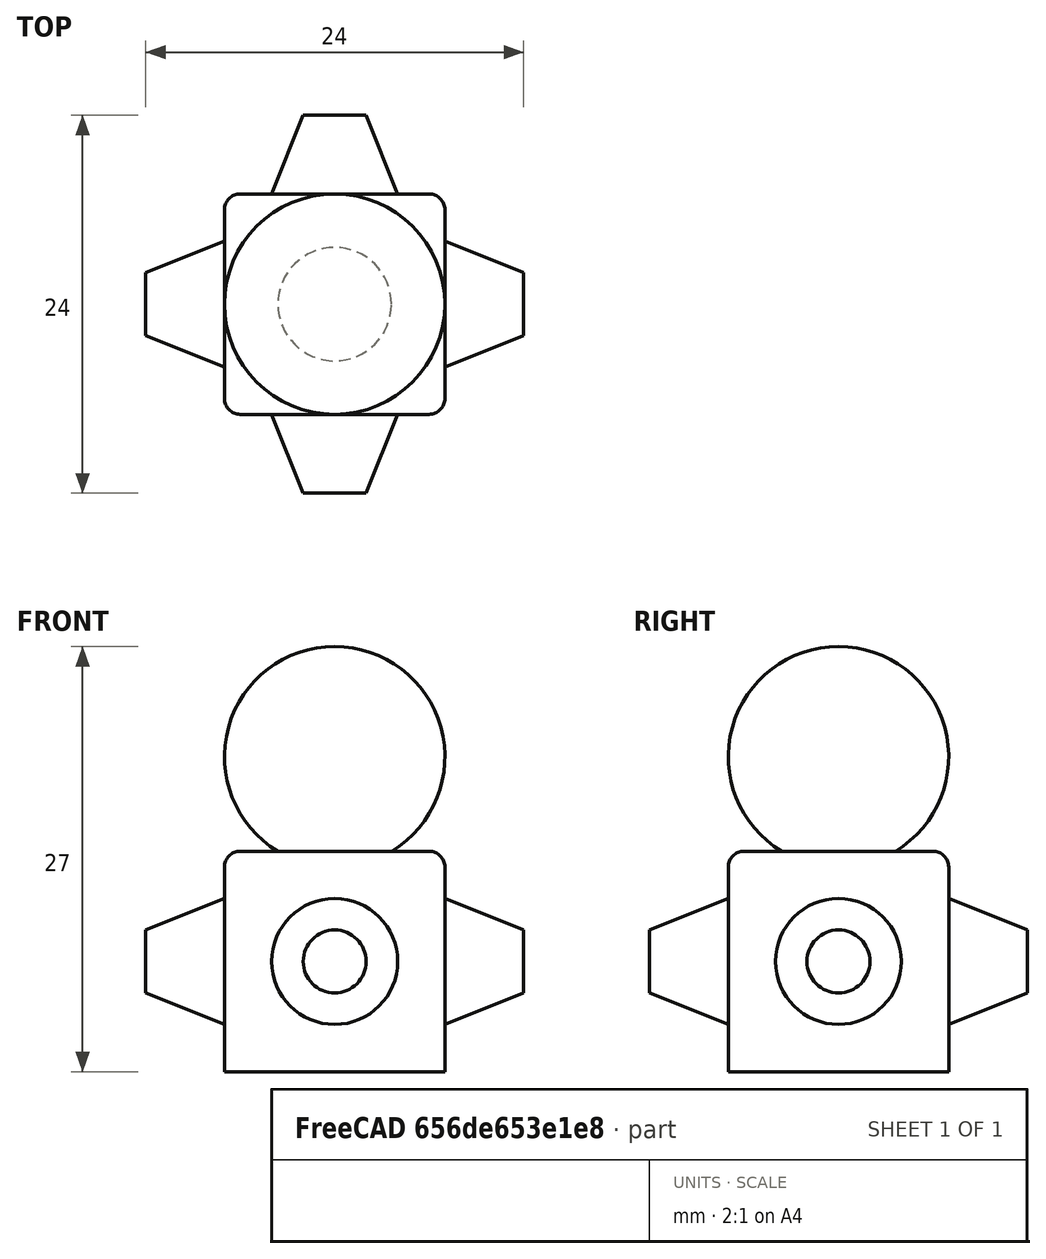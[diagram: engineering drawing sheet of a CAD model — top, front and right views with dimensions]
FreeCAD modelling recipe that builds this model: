
FCSTD DOCUMENT  (FreeCAD 0.20R)
Label: SpikePawn2
License: All rights reserved
LicenseURL: http://en.wikipedia.org/wiki/All_rights_reserved
objects: Part::Cone×4, Part::Box×1, Part::Sphere×1, Part::Fillet×1, Part::MultiFuse×1
note: 8 computed .brp shape members not serialized (recipe doc carries the construction recipe); baked Part::Feature solids carry a one-line shape summary decoded from their .brp

FEATURE [Part::Box] Box  label="Cube"
  AttacherType = Attacher::AttachEngine3D
  Height = 14
  Length = 14
  Width = 14
FEATURE [Part::Sphere] Sphere
  Angle1 = -90
  Angle2 = 90
  Angle3 = 360
  AttacherType = Attacher::AttachEngine3D
  Placement = pos=(7,7,20) rot=(0,0,1;0rad)
  Radius = 7
FEATURE [Part::Cone] Cone
  Angle = 360
  AttacherType = Attacher::AttachEngine3D
  AttachmentOffset = pos=(-7,7,-5) rot=(0,0,1;0rad)
  Height = 5
  MapMode = 5
  Placement = pos=(7,-5,7) rot=(0,0.707107,0.707107;3.14159rad)
  Radius1 = 2
  Radius2 = 4
  Support = -> [Box]
FEATURE [Part::Cone] Cone001
  Angle = 360
  AttacherType = Attacher::AttachEngine3D
  AttachmentOffset = pos=(-7,7,-5) rot=(0,0,1;0rad)
  Height = 5
  MapMode = 5
  Placement = pos=(19,7,7) rot=(0.57735,-0.57735,-0.57735;2.0944rad)
  Radius1 = 2
  Radius2 = 4
  Support = -> [Box]
FEATURE [Part::Cone] Cone002
  Angle = 360
  AttacherType = Attacher::AttachEngine3D
  AttachmentOffset = pos=(7,7,-5) rot=(0,0,1;0rad)
  Height = 5
  MapMode = 5
  Placement = pos=(7,19,7) rot=(1,0,0;1.5708rad)
  Radius1 = 2
  Radius2 = 4
  Support = -> [Box]
FEATURE [Part::Cone] Cone003
  Angle = 360
  AttacherType = Attacher::AttachEngine3D
  AttachmentOffset = pos=(7,7,-5) rot=(0,0,1;0rad)
  Height = 5
  MapMode = 5
  Placement = pos=(-5,7,7) rot=(0.57735,0.57735,0.57735;2.0944rad)
  Radius1 = 2
  Radius2 = 4
  Support = -> [Box]
FEATURE [Part::Fillet] Fillet
  Base = -> Box
  Edges = 8 edges r=1: [Edge1,Edge2,Edge3,Edge5,Edge6,Edge7,Edge10,Edge12]
FEATURE [Part::MultiFuse] Fusion
  Shapes = -> [Sphere,Cone,Cone001,Cone002,Cone003,Fillet]
